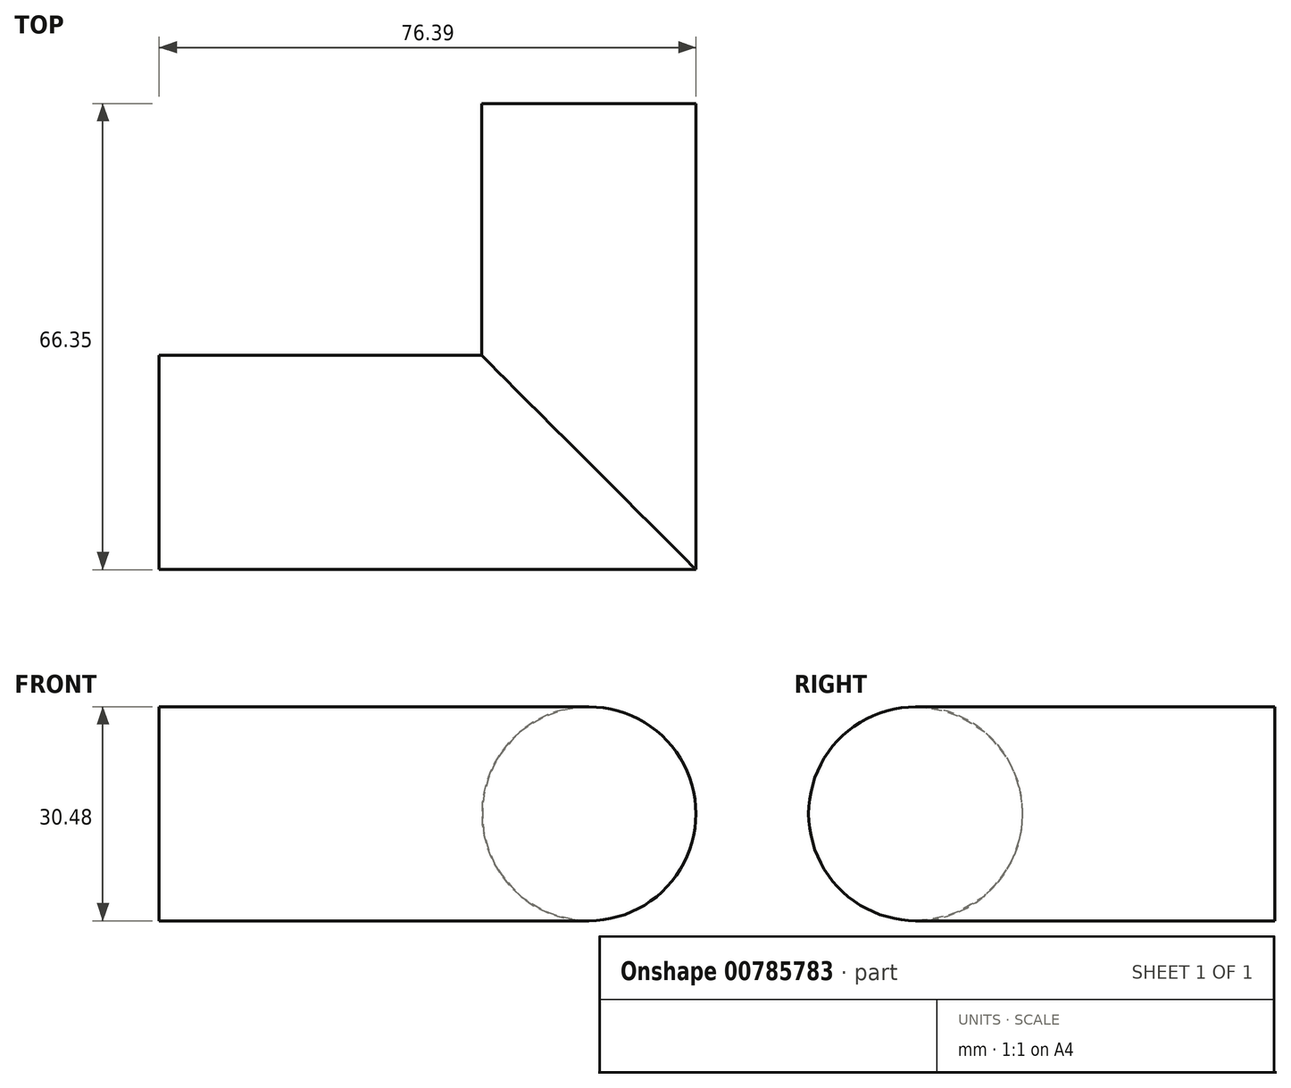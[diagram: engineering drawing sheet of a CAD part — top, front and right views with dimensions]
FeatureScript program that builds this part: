
annotation { "Feature Type Name" : "Feature", "Feature Type Description" : "" }
export const myFeature = defineFeature(function(context is Context, id is Id, definition is map)
    precondition{}
    {
        {
            var Q0;
            Q0=qCreatedBy(makeId("Top.planeOp"),FACE);
            var sketch = newSketch(context, id + "F0", { "sketchPlane" : qUnion([Q0])});
            skLineSegment(sketch, "E0", {"start": v(-60.03, -50) * mm, "end": v(0, -50) * mm});
            skLineSegment(sketch, "E1", {"start": v(0, -50) * mm, "end": v(0, 0) * mm});
            skSolve(sketch);
        }
        {
            var Q0;
            Q0=qCreatedBy(makeId("Right.planeOp"),FACE);
            var sketch = newSketch(context, id + "F1", { "sketchPlane" : qUnion([Q0])});
            skCircle(sketch, "E2", {"center": v(-51.1, 0) * mm, "radius": 15.24 * mm});
            skSolve(sketch);
        }
        {
            var Q0;
            Q0=makeQuery(id+"F1.imprint","IMPRINT",FACE,{"disambiguationData":[TD([[makeQuery(id+"F1.imprint","IMPRINT",EDGE,{"derivedFrom":sQuery(id+"F1.wireOp",EDGE,"E2")}),1.0]])]});
            var Q1;
            Q1=sQuery(id+"F1.wireOp",EDGE,"E2");
            var Q2;
            Q2=sQuery(id+"F0.wireOp",EDGE,"E0");
            var Q3;
            Q3=sQuery(id+"F0.wireOp",EDGE,"E1");
            sweep(context, id + "F2", {"profiles" : qUnion([Q0]), "surfaceProfiles" : qUnion([Q1]), "path" : qUnion([Q2, Q3])});
        }
    });
